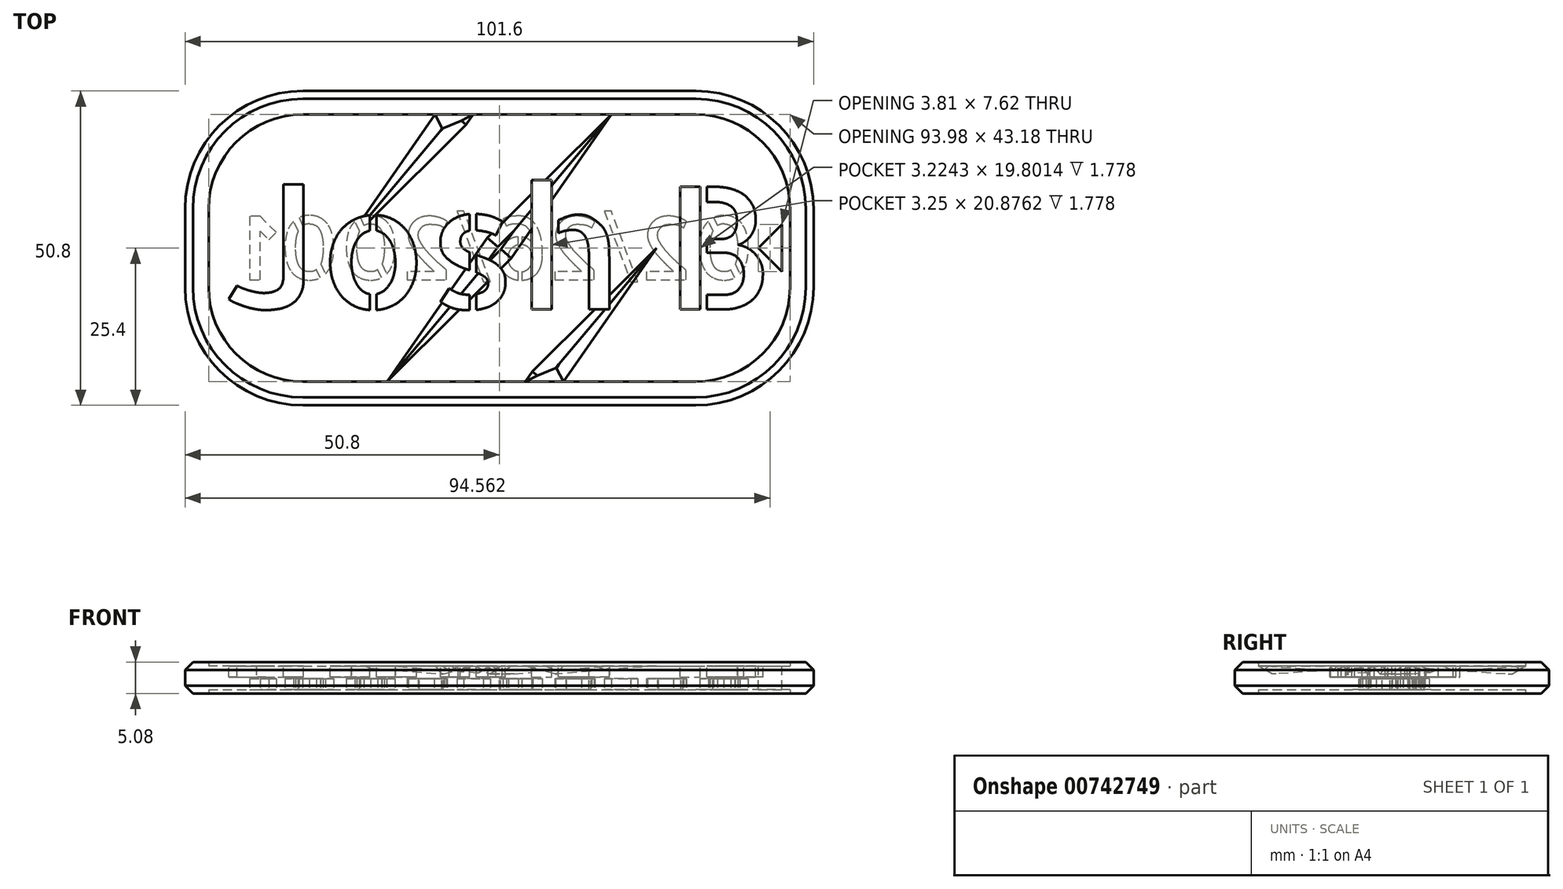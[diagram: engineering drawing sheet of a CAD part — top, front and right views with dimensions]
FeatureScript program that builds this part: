
annotation { "Feature Type Name" : "Feature", "Feature Type Description" : "" }
export const myFeature = defineFeature(function(context is Context, id is Id, definition is map)
    precondition{}
    {
        {
            var Q0;
            Q0=qCreatedBy(makeId("Top.planeOp"),FACE);
            var sketch = newSketch(context, id + "F0", { "sketchPlane" : qUnion([Q0])});
            skLineSegment(sketch, "E0.bottom", {"start": v(-31.75, 25.4) * mm, "end": v(31.75, 25.4) * mm});
            skLineSegment(sketch, "E0.top", {"start": v(-31.75, -25.4) * mm, "end": v(31.75, -25.4) * mm});
            skLineSegment(sketch, "E0.left", {"start": v(-50.8, 6.35) * mm, "end": v(-50.8, -6.35) * mm});
            skLineSegment(sketch, "E0.right", {"start": v(50.8, 6.35) * mm, "end": v(50.8, -6.35) * mm});
            skPoint(sketch, "E0.middle", {"position": v(0, 0) * mm});
            skPoint(sketch, "E1.visualSharp", {"position": v(-50.8, -25.4) * mm});
            skArc(sketch, "E1.filletArc", {"start": v(-50.8, -6.35) * mm, "mid": v(-45.22, -19.82) * mm, "end": v(-31.75, -25.4) * mm});
            skPoint(sketch, "E2.visualSharp", {"position": v(-50.8, 25.4) * mm});
            skArc(sketch, "E2.filletArc", {"start": v(-31.75, 25.4) * mm, "mid": v(-45.22, 19.82) * mm, "end": v(-50.8, 6.35) * mm});
            skPoint(sketch, "E3.visualSharp", {"position": v(50.8, 25.4) * mm});
            skArc(sketch, "E3.filletArc", {"start": v(50.8, 6.35) * mm, "mid": v(45.22, 19.82) * mm, "end": v(31.75, 25.4) * mm});
            skPoint(sketch, "E4.visualSharp", {"position": v(50.8, -25.4) * mm});
            skArc(sketch, "E4.filletArc", {"start": v(31.75, -25.4) * mm, "mid": v(45.22, -19.82) * mm, "end": v(50.8, -6.35) * mm});
            skLineSegment(sketch, "E5.0", {"start": v(-31.75, 21.6) * mm, "end": v(31.75, 21.6) * mm});
            skArc(sketch, "E5.1", {"start": v(47, 6.35) * mm, "mid": v(42.53, 17.13) * mm, "end": v(31.75, 21.6) * mm});
            skArc(sketch, "E5.2", {"start": v(-31.75, 21.6) * mm, "mid": v(-42.53, 17.13) * mm, "end": v(-47, 6.35) * mm});
            skLineSegment(sketch, "E5.3", {"start": v(47, 6.35) * mm, "end": v(47, -6.35) * mm});
            skLineSegment(sketch, "E5.4", {"start": v(-47, 6.35) * mm, "end": v(-47, -6.35) * mm});
            skArc(sketch, "E5.5", {"start": v(-47, -6.35) * mm, "mid": v(-42.53, -17.13) * mm, "end": v(-31.75, -21.6) * mm});
            skLineSegment(sketch, "E5.6", {"start": v(-31.75, -21.6) * mm, "end": v(31.75, -21.6) * mm});
            skArc(sketch, "E5.7", {"start": v(31.75, -21.6) * mm, "mid": v(42.53, -17.13) * mm, "end": v(47, -6.35) * mm});
            skSolve(sketch);
        }
        {
            var Q0;
            Q0=makeQuery(id+"F0.imprint","IMPRINT",FACE,{"disambiguationData":[TD([[makeQuery(id+"F0.imprint","IMPRINT",EDGE,{"derivedFrom":sQuery(id+"F0.wireOp",EDGE,"E5.0")}),-1.0]])]});
            extrude(context, id + "F1", {"entities" : qUnion([Q0]), "endBound" : BoundingType.SYMMETRIC, "depth" : 3.8 * mm, "offsetDistance" : 25.4 * mm});
        }
        {
            var Q0;
            Q0=makeQuery(id+"F0.imprint","IMPRINT",FACE,{"disambiguationData":[TD([[makeQuery(id+"F0.imprint","IMPRINT",EDGE,{"derivedFrom":sQuery(id+"F0.wireOp",EDGE,"E0.bottom")}),-1.0]])]});
            extrude(context, id + "F2", {"entities" : qUnion([Q0]), "operationType" : NewBodyOperationType.ADD, "endBound" : BoundingType.SYMMETRIC, "depth" : 5.08 * mm, "offsetDistance" : 25.4 * mm});
        }
        {
            var Q0;
            Q0=makeQuery(id+"F2.opExtrude","CAP_EDGE",EDGE,{"disambiguationData":[OSD([sQuery(id+"F0.wireOp",EDGE,"E1.filletArc")])],"isStart":false});
            var Q1;
            Q1=makeQuery(id+"F2.opExtrude","CAP_EDGE",EDGE,{"disambiguationData":[OSD([sQuery(id+"F0.wireOp",EDGE,"E0.top")])],"isStart":false});
            var Q2;
            Q2=makeQuery(id+"F2.opExtrude","CAP_EDGE",EDGE,{"disambiguationData":[OSD([sQuery(id+"F0.wireOp",EDGE,"E4.filletArc")])],"isStart":false});
            var Q3;
            Q3=makeQuery(id+"F2.opExtrude","CAP_EDGE",EDGE,{"disambiguationData":[OSD([sQuery(id+"F0.wireOp",EDGE,"E0.right")])],"isStart":false});
            var Q4;
            Q4=makeQuery(id+"F2.opExtrude","CAP_EDGE",EDGE,{"disambiguationData":[OSD([sQuery(id+"F0.wireOp",EDGE,"E3.filletArc")])],"isStart":false});
            var Q5;
            Q5=makeQuery(id+"F2.opExtrude","CAP_EDGE",EDGE,{"disambiguationData":[OSD([sQuery(id+"F0.wireOp",EDGE,"E0.bottom")])],"isStart":false});
            var Q6;
            Q6=makeQuery(id+"F2.opExtrude","CAP_EDGE",EDGE,{"disambiguationData":[OSD([sQuery(id+"F0.wireOp",EDGE,"E2.filletArc")])],"isStart":false});
            var Q7;
            Q7=makeQuery(id+"F2.opExtrude","CAP_EDGE",EDGE,{"disambiguationData":[OSD([sQuery(id+"F0.wireOp",EDGE,"E0.left")])],"isStart":false});
            var Q8;
            Q8=makeQuery(id+"F2.opExtrude","CAP_EDGE",EDGE,{"disambiguationData":[OSD([sQuery(id+"F0.wireOp",EDGE,"E1.filletArc")])],"isStart":true});
            var Q9;
            Q9=makeQuery(id+"F2.opExtrude","CAP_EDGE",EDGE,{"disambiguationData":[OSD([sQuery(id+"F0.wireOp",EDGE,"E0.left")])],"isStart":true});
            var Q10;
            Q10=makeQuery(id+"F2.opExtrude","CAP_EDGE",EDGE,{"disambiguationData":[OSD([sQuery(id+"F0.wireOp",EDGE,"E2.filletArc")])],"isStart":true});
            var Q11;
            Q11=makeQuery(id+"F2.opExtrude","CAP_EDGE",EDGE,{"disambiguationData":[OSD([sQuery(id+"F0.wireOp",EDGE,"E0.bottom")])],"isStart":true});
            var Q12;
            Q12=makeQuery(id+"F2.opExtrude","CAP_EDGE",EDGE,{"disambiguationData":[OSD([sQuery(id+"F0.wireOp",EDGE,"E3.filletArc")])],"isStart":true});
            var Q13;
            Q13=makeQuery(id+"F2.opExtrude","CAP_EDGE",EDGE,{"disambiguationData":[OSD([sQuery(id+"F0.wireOp",EDGE,"E0.right")])],"isStart":true});
            var Q14;
            Q14=makeQuery(id+"F2.opExtrude","CAP_EDGE",EDGE,{"disambiguationData":[OSD([sQuery(id+"F0.wireOp",EDGE,"E4.filletArc")])],"isStart":true});
            var Q15;
            Q15=makeQuery(id+"F2.opExtrude","CAP_EDGE",EDGE,{"disambiguationData":[OSD([sQuery(id+"F0.wireOp",EDGE,"E0.top")])],"isStart":true});
            chamfer(context, id + "F3", {"entities" : qUnion([Q0, Q1, Q2, Q3, Q4, Q5, Q6, Q7, Q8, Q9, Q10, Q11, Q12, Q13, Q14, Q15]), "width" : 1.27 * mm, "tangentPropagation" : true});
        }
        {
            var Q0;
            Q0=makeQuery(id+"F1.opExtrude","CAP_FACE",FACE,{"disambiguationData":[OSD([sQuery(id+"F0.wireOp",EDGE,"E5.0"),sQuery(id+"F0.wireOp",EDGE,"E5.1"),sQuery(id+"F0.wireOp",EDGE,"E5.2"),sQuery(id+"F0.wireOp",EDGE,"E5.3"),sQuery(id+"F0.wireOp",EDGE,"E5.4"),sQuery(id+"F0.wireOp",EDGE,"E5.5"),sQuery(id+"F0.wireOp",EDGE,"E5.6"),sQuery(id+"F0.wireOp",EDGE,"E5.7")])],"isStart":false});
            var sketch = newSketch(context, id + "F4", { "sketchPlane" : qUnion([Q0])});
            skText(sketch, "E6", { "text": "Josh B", "fontName": "AllertaStencil-Regular.ttf"});
            skLineSegment(sketch, "E7", {"start": v(-21.03, -2.29) * mm, "end": v(-19.76, -2.29) * mm});
            skLineSegment(sketch, "E8", {"start": v(-20.4, -9.9) * mm, "end": v(-20.4, 5.33) * mm});
            skLineSegment(sketch, "E9", {"start": v(-21.03, -2.29) * mm, "end": v(-21.03, -1.9) * mm});
            skLineSegment(sketch, "E10", {"start": v(-21.03, -2.29) * mm, "end": v(-21.03, -2.67) * mm});
            skLineSegment(sketch, "E11", {"start": v(-24.12, -1.9) * mm, "end": v(-24.12, -2.67) * mm});
            skLineSegment(sketch, "E12", {"start": v(-16.36, -1.9) * mm, "end": v(-16.36, -2.67) * mm});
            const initialGuessF4  = {"E6": [-0.04445, -0.0099, 1, 0, 0.01981]};
            skSetInitialGuess(sketch, initialGuessF4);
            skSolve(sketch);
        }
        {
            var Q0;
            Q0 = qSketchRegion(id + "F4", true);
            extrude(context, id + "F5", {"entities" : qUnion([Q0]), "operationType" : NewBodyOperationType.REMOVE, "oppositeDirection" : true, "depth" : 1.78 * mm, "offsetDistance" : 25.4 * mm});
        }
        {
            var Q0;
            Q0=makeQuery(id+"F1.opExtrude","CAP_FACE",FACE,{"disambiguationData":[OSD([sQuery(id+"F0.wireOp",EDGE,"E5.0"),sQuery(id+"F0.wireOp",EDGE,"E5.1"),sQuery(id+"F0.wireOp",EDGE,"E5.2"),sQuery(id+"F0.wireOp",EDGE,"E5.3"),sQuery(id+"F0.wireOp",EDGE,"E5.4"),sQuery(id+"F0.wireOp",EDGE,"E5.5"),sQuery(id+"F0.wireOp",EDGE,"E5.6"),sQuery(id+"F0.wireOp",EDGE,"E5.7")])],"isStart":false});
            var sketch = newSketch(context, id + "F6", { "sketchPlane" : qUnion([Q0])});
            skLineSegment(sketch, "E13", {"start": v(0, 0) * mm, "end": v(-18.12, -21.6) * mm});
            skLineSegment(sketch, "E14", {"start": v(0, 0) * mm, "end": v(18.12, 21.6) * mm});
            skPoint(sketch, "E15.end.orphan", {"position": v(-25.4, 0) * mm});
            skPoint(sketch, "E15.start.orphan", {"position": v(0, 30.27) * mm});
            skLineSegment(sketch, "E16", {"start": v(-25.4, 0) * mm, "end": v(-7.28, 21.6) * mm});
            skLineSegment(sketch, "E17", {"start": v(7.28, -21.6) * mm, "end": v(25.4, 0) * mm});
            skLineSegment(sketch, "E18", {"start": v(-7.28, 21.6) * mm, "end": v(-5.34, 19.96) * mm});
            skLineSegment(sketch, "E19", {"start": v(0, 30.27) * mm, "end": v(10.83, 43.18) * mm, "construction": true});
            skLineSegment(sketch, "E20", {"start": v(-25.4, 0) * mm, "end": v(-5.34, 19.96) * mm});
            skLineSegment(sketch, "E21", {"start": v(-5.34, 19.96) * mm, "end": v(-4.2, 21.6) * mm});
            skLineSegment(sketch, "E22", {"start": v(-25.4, 0) * mm, "end": v(-10.37, 21.6) * mm});
            skLineSegment(sketch, "E23", {"start": v(-7.28, 21.6) * mm, "end": v(-10.37, 21.6) * mm});
            skPoint(sketch, "E24.end.orphan", {"position": v(-9.23, 23.22) * mm});
            skLineSegment(sketch, "E25", {"start": v(-4.2, 21.6) * mm, "end": v(-7.28, 21.6) * mm});
            skLineSegment(sketch, "E26", {"start": v(0, 0) * mm, "end": v(1.95, -1.63) * mm});
            skLineSegment(sketch, "E27", {"start": v(0, 0) * mm, "end": v(-1.95, 1.63) * mm});
            skLineSegment(sketch, "E28", {"start": v(-1.95, 1.63) * mm, "end": v(-18.12, -21.6) * mm});
            skLineSegment(sketch, "E29", {"start": v(-18.12, -21.6) * mm, "end": v(1.95, -1.63) * mm});
            skLineSegment(sketch, "E30", {"start": v(-1.95, 1.63) * mm, "end": v(18.12, 21.6) * mm});
            skLineSegment(sketch, "E31", {"start": v(18.12, 21.6) * mm, "end": v(1.95, -1.63) * mm});
            skLineSegment(sketch, "E32", {"start": v(7.28, -21.6) * mm, "end": v(5.34, -19.96) * mm});
            skLineSegment(sketch, "E33", {"start": v(5.34, -19.96) * mm, "end": v(4.2, -21.6) * mm});
            skLineSegment(sketch, "E34", {"start": v(5.34, -19.96) * mm, "end": v(25.4, 0) * mm});
            skLineSegment(sketch, "E35", {"start": v(10.37, -21.6) * mm, "end": v(25.4, 0) * mm});
            skLineSegment(sketch, "E36", {"start": v(7.28, -21.6) * mm, "end": v(10.37, -21.6) * mm});
            skLineSegment(sketch, "E37", {"start": v(7.28, -21.6) * mm, "end": v(4.2, -21.6) * mm});
            skSolve(sketch);
        }
        {
            var Q0;
            Q0 = qSketchRegion(id + "F6", true);
            extrude(context, id + "F7", {"entities" : qUnion([Q0]), "operationType" : NewBodyOperationType.REMOVE, "oppositeDirection" : true, "depth" : 1.27 * mm, "offsetDistance" : 25.4 * mm, "hasDraft" : true, "draftAngle" : 60 * degree, "draftPullDirection" : true});
        }
        {
            var Q0;
            {var subQ0=sQuery(id+"F0.wireOp",EDGE,"E5.7");var subQ1=sQuery(id+"F0.wireOp",EDGE,"E5.6");var subQ2=sQuery(id+"F0.wireOp",EDGE,"E5.3");var subQ3=sQuery(id+"F0.wireOp",EDGE,"E5.1");var subQ4=sQuery(id+"F0.wireOp",EDGE,"E5.0");var subQ5=makeQuery(id+"F1.opExtrude","CAP_FACE",FACE,{"disambiguationData":[OSD([subQ4,subQ3,sQuery(id+"F0.wireOp",EDGE,"E5.2"),subQ2,sQuery(id+"F0.wireOp",EDGE,"E5.4"),sQuery(id+"F0.wireOp",EDGE,"E5.5"),subQ1,subQ0])],"isStart":false});Q0=makeQuery(id+"F7.boolean.opBoolean","SPLIT",FACE,{"disambiguationData":[TD([makeQuery(id+"F2.opExtrude","SWEPT_FACE",FACE,{"disambiguationData":[OSD([subQ3])]})])],"derivedFrom":subQ5});}
            var sketch = newSketch(context, id + "F8", { "sketchPlane" : qUnion([Q0])});
            skLineSegment(sketch, "E38", {"start": v(47, 0) * mm, "end": v(41.85, 0) * mm, "construction": true});
            skLineSegment(sketch, "E39", {"start": v(45.67, 0) * mm, "end": v(45.67, 3.81) * mm});
            skLineSegment(sketch, "E40", {"start": v(45.67, 0) * mm, "end": v(45.67, -3.81) * mm});
            skLineSegment(sketch, "E41", {"start": v(45.67, -3.81) * mm, "end": v(41.86, 0) * mm});
            skLineSegment(sketch, "E42", {"start": v(41.86, 0) * mm, "end": v(45.67, 3.81) * mm});
            skSolve(sketch);
        }
        {
            var Q0;
            Q0 = qSketchRegion(id + "F8", true);
            extrude(context, id + "F9", {"entities" : qUnion([Q0]), "operationType" : NewBodyOperationType.REMOVE, "oppositeDirection" : true, "depth" : 25.4 * mm, "offsetDistance" : 25.4 * mm});
        }
        {
            var Q0;
            Q0=makeQuery(id+"F1.opExtrude","CAP_FACE",FACE,{"disambiguationData":[OSD([sQuery(id+"F0.wireOp",EDGE,"E5.0"),sQuery(id+"F0.wireOp",EDGE,"E5.1"),sQuery(id+"F0.wireOp",EDGE,"E5.2"),sQuery(id+"F0.wireOp",EDGE,"E5.3"),sQuery(id+"F0.wireOp",EDGE,"E5.4"),sQuery(id+"F0.wireOp",EDGE,"E5.5"),sQuery(id+"F0.wireOp",EDGE,"E5.6"),sQuery(id+"F0.wireOp",EDGE,"E5.7")])],"isStart":true});
            var sketch = newSketch(context, id + "F10", { "sketchPlane" : qUnion([Q0])});
            skText(sketch, "E43", { "text": "02/26/2001", "fontName": "AllertaStencil-Regular.ttf"});
            skLineSegment(sketch, "E44", {"start": v(41.28, 5.12) * mm, "end": v(39.87, 5.12) * mm});
            const initialGuessF10  = {"E43": [0.04128, 0.00512, -1, 0, 0.01025]};
            skSetInitialGuess(sketch, initialGuessF10);
            skSolve(sketch);
        }
        {
            var Q0;
            Q0 = qSketchRegion(id + "F10", true);
            extrude(context, id + "F11", {"entities" : qUnion([Q0]), "operationType" : NewBodyOperationType.REMOVE, "oppositeDirection" : true, "depth" : 1.78 * mm, "offsetDistance" : 25.4 * mm});
        }
    });
